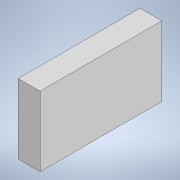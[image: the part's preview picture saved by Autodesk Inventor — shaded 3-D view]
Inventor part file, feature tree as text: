
AUTODESK INVENTOR PART (.ipt)
format: ipt  version: 2020 (Build 240168000, 168)  size: 86,528 bytes
history: native  units: mm
features: extrude x1, sketch x1
ambient origin geometry x8: Origin, YZ Plane, XZ Plane, XY Plane, X Axis, Y Axis, Z Axis, Center Point
bodies: Solide1 (feature_tree)
feature tree (2):
  extrude  "Extrusion1"  Depth=22.0mm
  sketch  "Esquisse1"
